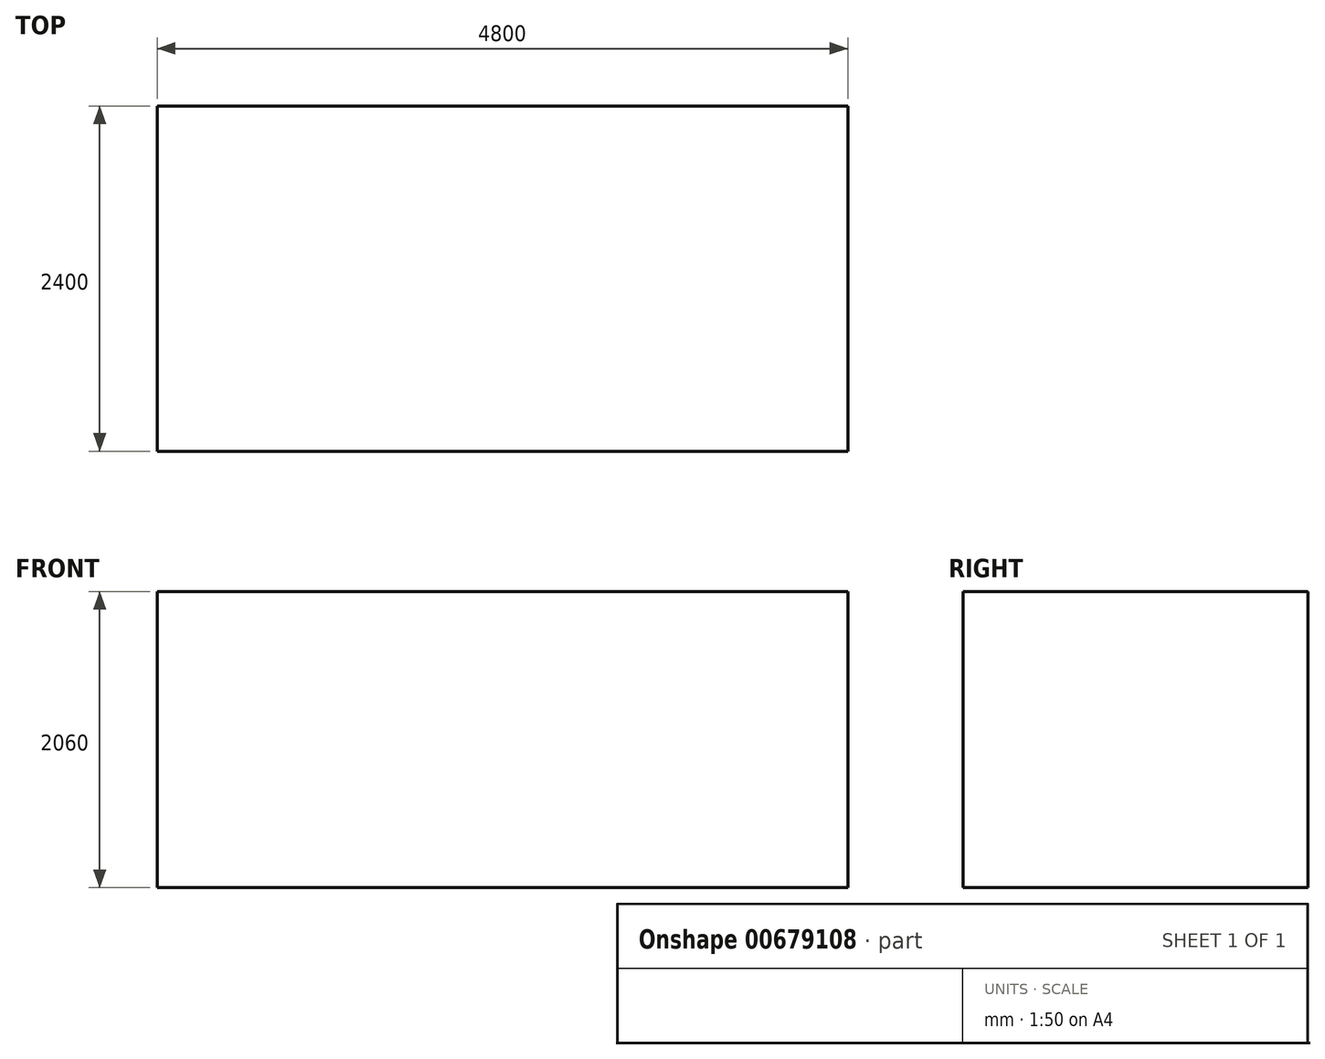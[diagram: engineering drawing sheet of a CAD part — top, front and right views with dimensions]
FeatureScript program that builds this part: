
annotation { "Feature Type Name" : "Feature", "Feature Type Description" : "" }
export const myFeature = defineFeature(function(context is Context, id is Id, definition is map)
    precondition{}
    {
        {
            var Q0;
            Q0=qCreatedBy(makeId("Top.planeOp"),FACE);
            var sketch = newSketch(context, id + "F0", { "sketchPlane" : qUnion([Q0])});
            skLineSegment(sketch, "E0.bottom", {"start": v(-2384.8, 1639.75) * mm, "end": v(2415.2, 1639.75) * mm});
            skLineSegment(sketch, "E0.top", {"start": v(-2384.8, -760.25) * mm, "end": v(2415.2, -760.25) * mm});
            skLineSegment(sketch, "E0.left", {"start": v(-2384.8, 1639.75) * mm, "end": v(-2384.8, -760.25) * mm});
            skLineSegment(sketch, "E0.right", {"start": v(2415.2, 1639.75) * mm, "end": v(2415.2, -760.25) * mm});
            skSolve(sketch);
        }
        {
            var Q0;
            Q0 = qSketchRegion(id + "F0", true);
            extrude(context, id + "F1", {"entities" : qUnion([Q0]), "depth" : 2060 * mm, "offsetDistance" : 25 * mm});
        }
    });
